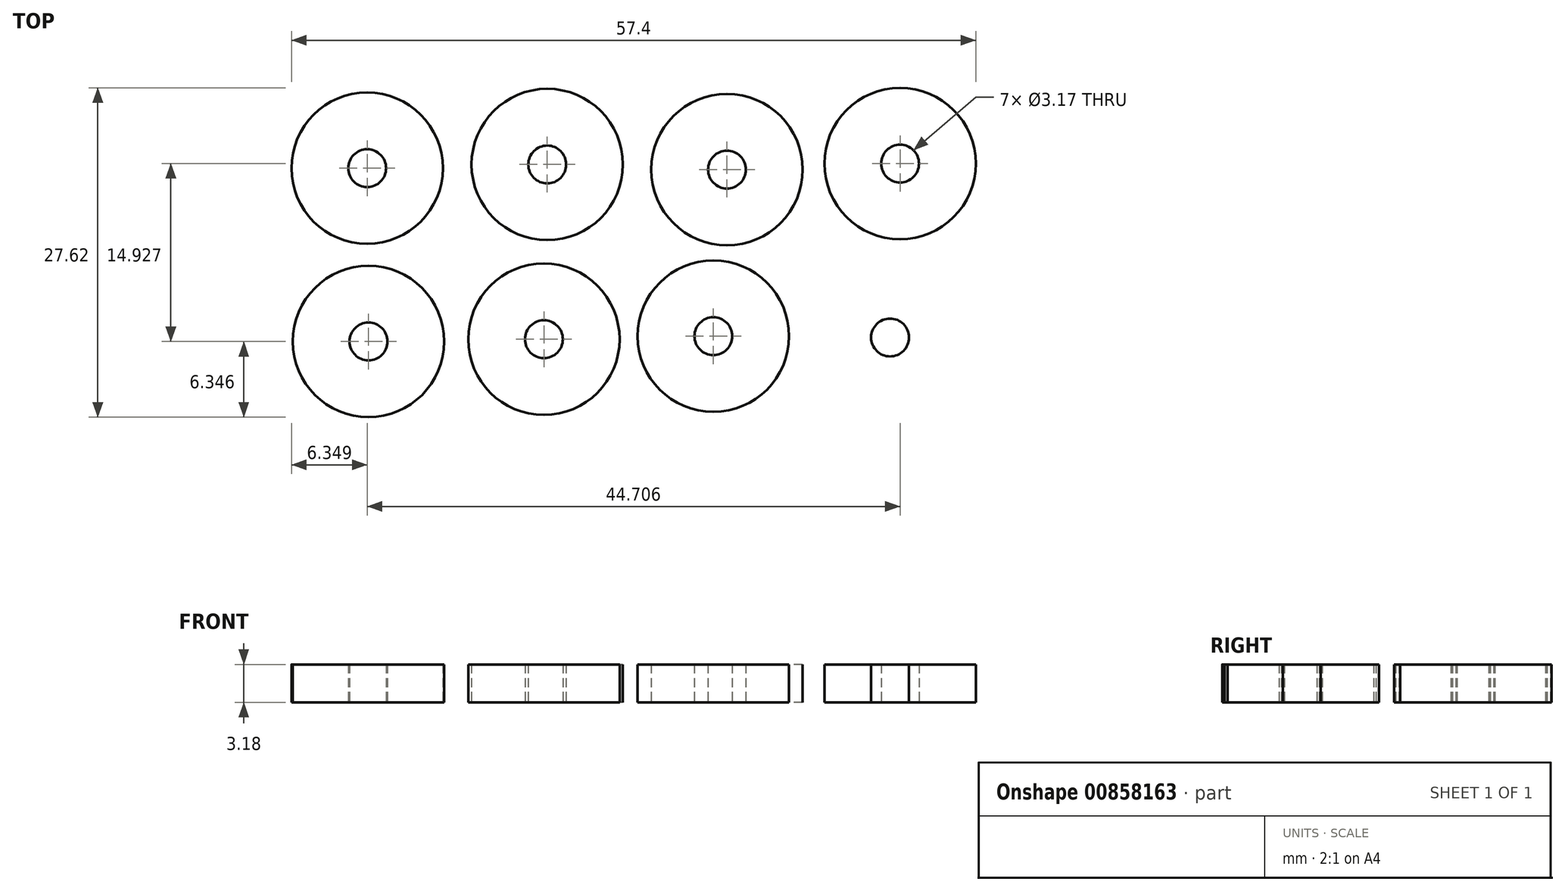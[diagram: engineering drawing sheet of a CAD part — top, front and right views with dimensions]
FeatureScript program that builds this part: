
annotation { "Feature Type Name" : "Feature", "Feature Type Description" : "" }
export const myFeature = defineFeature(function(context is Context, id is Id, definition is map)
    precondition{}
    {
        {
            var Q0;
            Q0=qCreatedBy(makeId("Top.planeOp"),FACE);
            var sketch = newSketch(context, id + "F0", { "sketchPlane" : qUnion([Q0])});
            skCircle(sketch, "E0", {"center": v(-24.6, 9.6) * mm, "radius": 6.35 * mm});
            skCircle(sketch, "E1", {"center": v(-9.5, 9.91) * mm, "radius": 6.35 * mm});
            skCircle(sketch, "E2", {"center": v(5.58, 9.49) * mm, "radius": 6.35 * mm});
            skCircle(sketch, "E3", {"center": v(20.1, 10) * mm, "radius": 6.35 * mm});
            skCircle(sketch, "E4", {"center": v(-24.49, -4.93) * mm, "radius": 6.35 * mm});
            skCircle(sketch, "E5", {"center": v(4.44, -4.49) * mm, "radius": 6.35 * mm});
            skCircle(sketch, "E6", {"center": v(-9.78, -4.75) * mm, "radius": 6.35 * mm});
            skCircle(sketch, "E7", {"center": v(-24.6, 9.6) * mm, "radius": 1.59 * mm});
            skCircle(sketch, "E8", {"center": v(-9.5, 9.91) * mm, "radius": 1.59 * mm});
            skCircle(sketch, "E9", {"center": v(5.58, 9.49) * mm, "radius": 1.59 * mm});
            skCircle(sketch, "E10", {"center": v(20.1, 10) * mm, "radius": 1.59 * mm});
            skCircle(sketch, "E11", {"center": v(19.26, -4.6) * mm, "radius": 1.59 * mm});
            skCircle(sketch, "E12", {"center": v(4.44, -4.49) * mm, "radius": 1.59 * mm});
            skCircle(sketch, "E13", {"center": v(-9.78, -4.75) * mm, "radius": 1.59 * mm});
            skCircle(sketch, "E14", {"center": v(-24.49, -4.93) * mm, "radius": 1.59 * mm});
            skSolve(sketch);
        }
        {
            var Q0;
            Q0=qSketchRegion(id+"F0",true);
            extrude(context, id + "F1", {"entities" : qUnion([Q0]), "depth" : 3.17 * mm, "offsetDistance" : 25.4 * mm});
        }
    });
